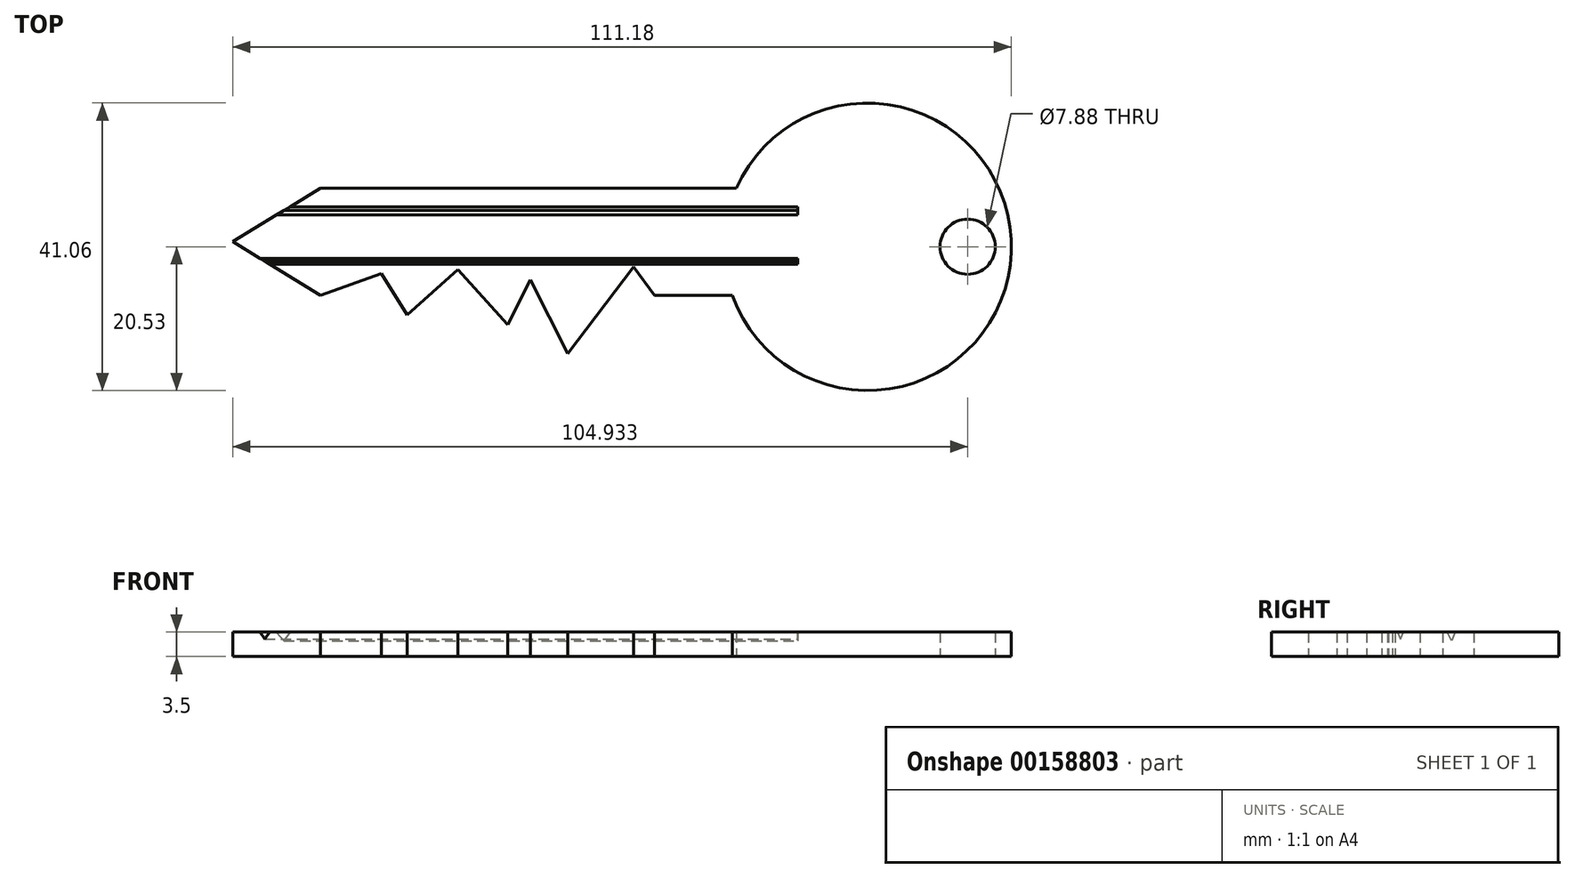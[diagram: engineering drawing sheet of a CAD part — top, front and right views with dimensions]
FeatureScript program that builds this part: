
annotation { "Feature Type Name" : "Feature", "Feature Type Description" : "" }
export const myFeature = defineFeature(function(context is Context, id is Id, definition is map)
    precondition{}
    {
        {
            var Q0;
            Q0=qCreatedBy(makeId("Top.planeOp"),FACE);
            var sketch = newSketch(context, id + "F0", { "sketchPlane" : qUnion([Q0])});
            skArc(sketch, "E0", {"start": v(-19.32, -6.95) * mm, "mid": v(20.52, -0.78) * mm, "end": v(-18.74, 8.39) * mm});
            skLineSegment(sketch, "E1.bottom", {"start": v(-19.32, -6.95) * mm, "end": v(-30.42, -6.95) * mm});
            skLineSegment(sketch, "E1.top", {"start": v(-18.74, 8.39) * mm, "end": v(-78.09, 8.39) * mm});
            skLineSegment(sketch, "E2", {"start": v(-78.09, 8.39) * mm, "end": v(-90.65, 0.72) * mm});
            skPoint(sketch, "E2.endSnap0", {"position": v(-78.09, 0.72) * mm});
            skLineSegment(sketch, "E3", {"start": v(-90.65, 0.72) * mm, "end": v(-78.09, -6.95) * mm});
            skCircle(sketch, "E4", {"center": v(14.28, 0) * mm, "radius": 3.94 * mm});
            skLineSegment(sketch, "E5", {"start": v(-78.09, -6.95) * mm, "end": v(-69.4, -3.8) * mm});
            skLineSegment(sketch, "E6", {"start": v(-69.4, -3.8) * mm, "end": v(-65.71, -9.72) * mm});
            skLineSegment(sketch, "E7", {"start": v(-65.71, -9.72) * mm, "end": v(-58.5, -3.25) * mm});
            skLineSegment(sketch, "E8", {"start": v(-58.5, -3.25) * mm, "end": v(-51.4, -11.16) * mm});
            skLineSegment(sketch, "E9", {"start": v(-51.4, -11.16) * mm, "end": v(-48.16, -4.73) * mm});
            skLineSegment(sketch, "E10", {"start": v(-48.16, -4.73) * mm, "end": v(-42.8, -15.26) * mm});
            skLineSegment(sketch, "E11", {"start": v(-42.8, -15.26) * mm, "end": v(-33.38, -2.88) * mm});
            skLineSegment(sketch, "E12", {"start": v(-33.38, -2.88) * mm, "end": v(-30.42, -6.95) * mm});
            skPoint(sketch, "E13.orphan", {"position": v(0, -6.95) * mm});
            skSolve(sketch);
        }
        {
            var Q0;
            Q0=makeQuery(id+"F0.imprint","IMPRINT",FACE,{"disambiguationData":[TD([[makeQuery(id+"F0.imprint","IMPRINT",EDGE,{"derivedFrom":sQuery(id+"F0.wireOp",EDGE,"E0")}),1.0]])]});
            extrude(context, id + "F1", {"entities" : qUnion([Q0]), "depth" : 3.5 * mm});
        }
        {
            var Q0;
            Q0=qCreatedBy(makeId("Right.planeOp"),FACE);
            cPlane(context, id + "F2", {"entities" : qUnion([Q0]), "cplaneType" : CPlaneType.OFFSET, "offset" : 10 * mm, "oppositeDirection" : true, "width" : 150 * mm, "height" : 150 * mm});
        }
        {
            var Q0;
            Q0=qCreatedBy(id+"F2.planeOp",FACE);
            var sketch = newSketch(context, id + "F3", { "sketchPlane" : qUnion([Q0])});
            skLineSegment(sketch, "E14", {"start": v(6.99, 6.37) * mm, "end": v(5.19, 2.28) * mm});
            skLineSegment(sketch, "E15", {"start": v(5.19, 2.28) * mm, "end": v(2.65, 7.1) * mm});
            skLineSegment(sketch, "E16", {"start": v(2.65, 7.1) * mm, "end": v(6.99, 6.37) * mm});
            skLineSegment(sketch, "E17", {"start": v(-0.44, 6.5) * mm, "end": v(-4.14, 7.14) * mm});
            skLineSegment(sketch, "E18", {"start": v(-4.14, 7.14) * mm, "end": v(-2.07, 2.5) * mm});
            skLineSegment(sketch, "E19", {"start": v(-2.07, 2.5) * mm, "end": v(-0.44, 6.5) * mm});
            skSolve(sketch);
        }
        {
            var Q0;
            Q0=makeQuery(id+"F3.imprint","IMPRINT",FACE,{"disambiguationData":[TD([[makeQuery(id+"F3.imprint","IMPRINT",EDGE,{"derivedFrom":sQuery(id+"F3.wireOp",EDGE,"E14")}),-1.0]])]});
            var Q1;
            Q1=makeQuery(id+"F3.imprint","IMPRINT",FACE,{"disambiguationData":[TD([[makeQuery(id+"F3.imprint","IMPRINT",EDGE,{"derivedFrom":sQuery(id+"F3.wireOp",EDGE,"E17")}),1.0]])]});
            extrude(context, id + "F4", {"entities" : qUnion([Q0, Q1]), "operationType" : NewBodyOperationType.REMOVE, "oppositeDirection" : true, "depth" : 150 * mm});
        }
    });
